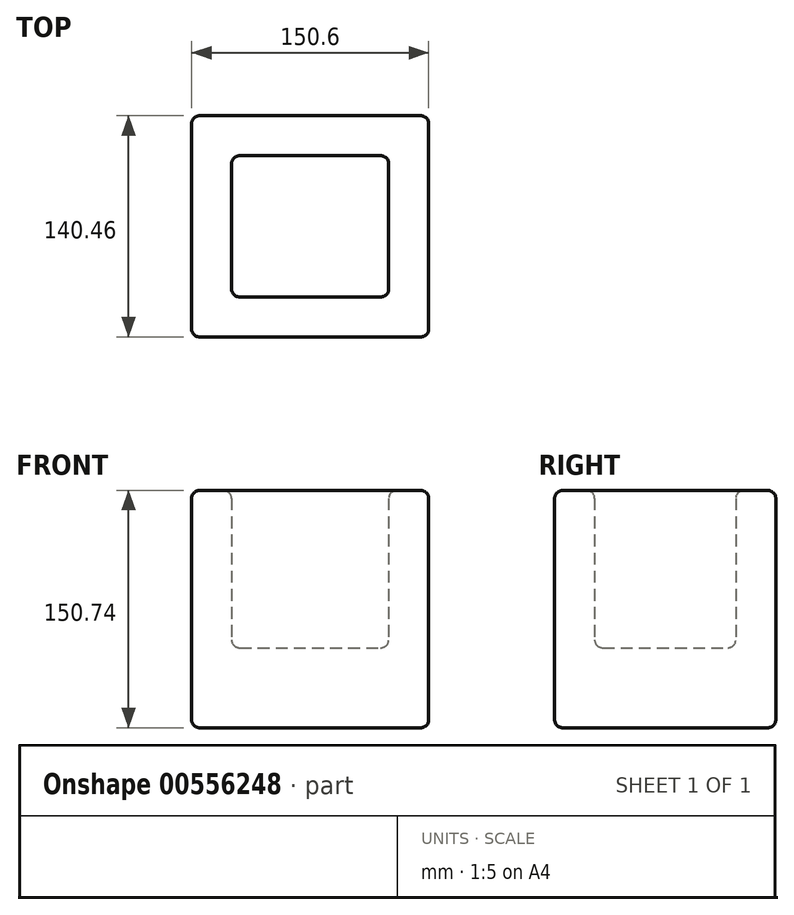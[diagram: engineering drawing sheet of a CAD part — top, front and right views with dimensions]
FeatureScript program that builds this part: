
annotation { "Feature Type Name" : "Feature", "Feature Type Description" : "" }
export const myFeature = defineFeature(function(context is Context, id is Id, definition is map)
    precondition{}
    {
        {
            var Q0;
            Q0=qCreatedBy(makeId("Front.planeOp"),FACE);
            var sketch = newSketch(context, id + "F0", { "sketchPlane" : qUnion([Q0])});
            skLineSegment(sketch, "E0.bottom", {"start": v(-75.3, 74.7) * mm, "end": v(75.3, 74.7) * mm});
            skLineSegment(sketch, "E0.top", {"start": v(-75.3, -76.05) * mm, "end": v(75.3, -76.05) * mm});
            skLineSegment(sketch, "E0.left", {"start": v(-75.3, 74.7) * mm, "end": v(-75.3, -76.05) * mm});
            skLineSegment(sketch, "E0.right", {"start": v(75.3, 74.7) * mm, "end": v(75.3, -76.05) * mm});
            skSolve(sketch);
        }
        {
            var Q0;
            Q0=qSketchRegion(id+"F0",true);
            extrude(context, id + "F1", {"entities" : qUnion([Q0]), "depth" : 140.46 * mm});
        }
        {
            var Q0;
            Q0=makeQuery(id+"F1.opExtrude","SWEPT_FACE",FACE,{"disambiguationData":[OSD([sQuery(id+"F0.wireOp",EDGE,"E0.bottom")])]});
            shell(context, id + "F2", {"entities" : qUnion([Q0]), "thickness" : 25.4 * mm});
        }
        {
            var Q0;
            Q0=makeQuery(id+"F2.opShell","OFFSET_FACE",FACE,{"disambiguationData":[OSD([sQuery(id+"F0.wireOp",EDGE,"E0.top")])]});
            extrude(context, id + "F3", {"entities" : qUnion([Q0]), "operationType" : NewBodyOperationType.ADD, "depth" : 25.4 * mm});
        }
        {
            var Q0;
            Q0=makeQuery(id+"F3.opExtrude","CAP_FACE",FACE,{"disambiguationData":[OSD([sQuery(id+"F0.wireOp",EDGE,"E0.top")])],"isStart":false});
            var sketch = newSketch(context, id + "F4", { "sketchPlane" : qUnion([Q0])});
            skSolve(sketch);
        }
        {
            var Q0;
            {var subQ0=sQuery(id+"F0.wireOp",EDGE,"E0.top");Q0=makeQuery(id+"F3.opExtrude","CAP_EDGE",EDGE,{"disambiguationData":[OSD([subQ0]),TDD([makeQuery(id+"F2.opShell","OFFSET_EDGE",EDGE,{"disambiguationData":[OSD([subQ0]),TDD([makeQuery(id+"F1.opExtrude","CAP_EDGE",EDGE,{"disambiguationData":[OSD([subQ0])],"isStart":true})])]})])],"isStart":false});}
            var Q1;
            Q1=makeQuery(id+"F3.opExtrude","CAP_FACE",FACE,{"disambiguationData":[OSD([sQuery(id+"F0.wireOp",EDGE,"E0.top")])],"isStart":false});
            var Q2;
            Q2=makeQuery(id+"F1.opExtrude","CAP_EDGE",EDGE,{"disambiguationData":[OSD([sQuery(id+"F0.wireOp",EDGE,"E0.bottom")])],"isStart":true});
            var Q3;
            Q3=makeQuery(id+"F1.opExtrude","SWEPT_FACE",FACE,{"disambiguationData":[OSD([sQuery(id+"F0.wireOp",EDGE,"E0.bottom")])]});
            var Q4;
            Q4=makeQuery(id+"F1.opExtrude","SWEPT_FACE",FACE,{"disambiguationData":[OSD([sQuery(id+"F0.wireOp",EDGE,"E0.top")])]});
            var Q5;
            Q5=makeQuery(id+"F1.opExtrude","CAP_FACE",FACE,{"disambiguationData":[OSD([sQuery(id+"F0.wireOp",EDGE,"E0.bottom"),sQuery(id+"F0.wireOp",EDGE,"E0.top"),sQuery(id+"F0.wireOp",EDGE,"E0.left"),sQuery(id+"F0.wireOp",EDGE,"E0.right")])],"isStart":false});
            var Q6;
            Q6=makeQuery(id+"F1.opExtrude","SWEPT_FACE",FACE,{"disambiguationData":[OSD([sQuery(id+"F0.wireOp",EDGE,"E0.right")])]});
            var Q7;
            Q7=makeQuery(id+"F1.opExtrude","CAP_FACE",FACE,{"disambiguationData":[OSD([sQuery(id+"F0.wireOp",EDGE,"E0.bottom"),sQuery(id+"F0.wireOp",EDGE,"E0.top"),sQuery(id+"F0.wireOp",EDGE,"E0.left"),sQuery(id+"F0.wireOp",EDGE,"E0.right")])],"isStart":true});
            var Q8;
            Q8=makeQuery(id+"F2.opShell","OFFSET_FACE",FACE,{"disambiguationData":[OSD([sQuery(id+"F0.wireOp",EDGE,"E0.left")])]});
            var Q9;
            Q9=makeQuery(id+"F2.opShell","OFFSET_FACE",FACE,{"disambiguationData":[OSD([sQuery(id+"F0.wireOp",EDGE,"E0.right")])]});
            fillet(context, id + "F5", {"entities" : qUnion([Q0, Q1, Q2, Q3, Q4, Q5, Q6, Q7, Q8, Q9]), "radius" : 5.08 * mm, "tangentPropagation" : true, "allowEdgeOverflow" : false});
        }
    });
